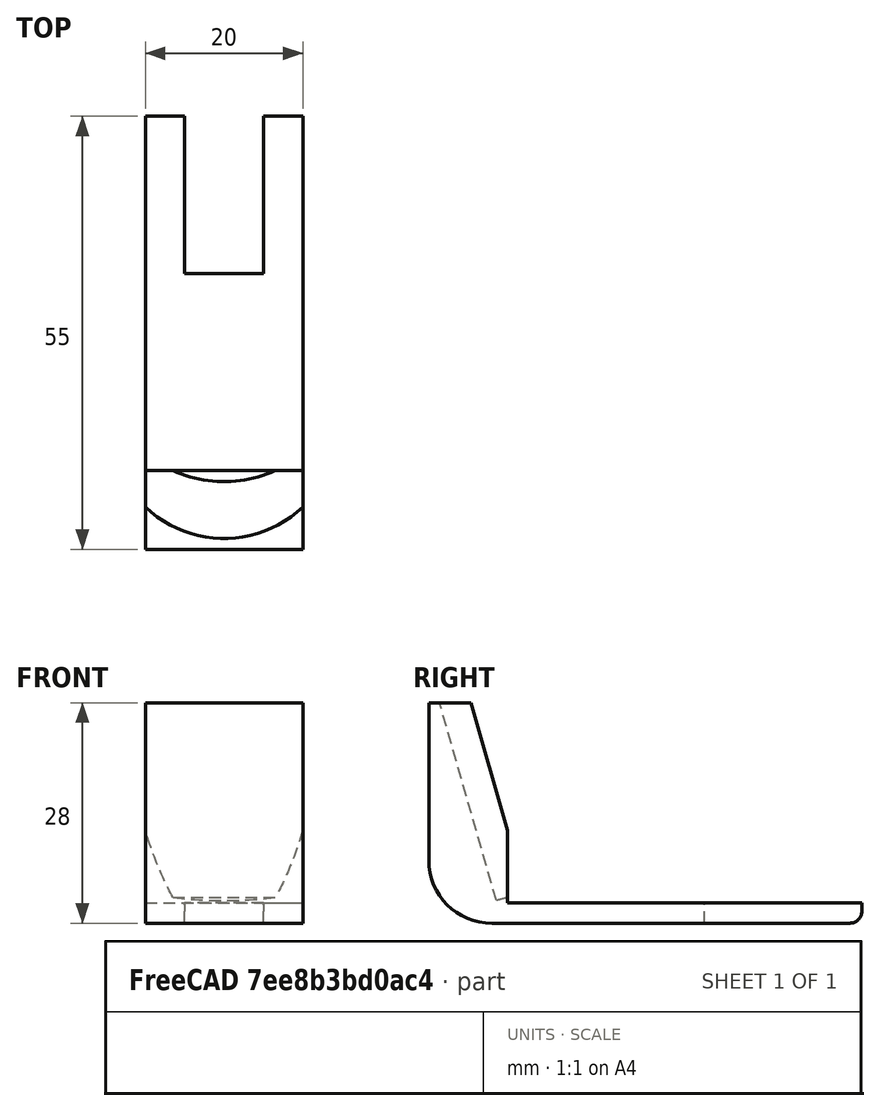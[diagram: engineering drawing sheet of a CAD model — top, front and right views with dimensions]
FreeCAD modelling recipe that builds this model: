
FCSTD DOCUMENT
Label: j-support_v1
objects: Part::Box×3, Part::Cut×2, Part::Fillet×2, Part::Cylinder×1, Part::Fuse×1
note: 9 computed .brp shape members not serialized (recipe doc carries the construction recipe); baked Part::Feature solids carry a one-line shape summary decoded from their .brp

FEATURE [Part::Box] Box  label="Box01"
  Height = 2.6
  Length = 20
  Width = 45
FEATURE [Part::Box] Box001  label="Box02"
  Height = 10
  Length = 10
  Placement = pos=(5,25,-3) rot=(0,0,1;0rad)
  Width = 25
FEATURE [Part::Cut] Cut  label="Patte"
  Base = -> Box
  Tool = -> Box001
FEATURE [Part::Box] Box002
  Height = 28
  Length = 20
  Placement = pos=(0,-10,0) rot=(0,0,1;0rad)
  Width = 10
FEATURE [Part::Fillet] Fillet
  Base = -> Box002
  Edges = 1 edges r=8: [Edge9]
FEATURE [Part::Cylinder] Cylinder
  Angle = 360
  Height = 27
  Placement = pos=(10,13,7) rot=(1,0,0;0.279252rad)
  Radius = 15
FEATURE [Part::Cut] Cut001
  Base = -> Fillet
  Tool = -> Cylinder
FEATURE [Part::Fuse] Fusion
  Base = -> Cut001
  Tool = -> Cut
FEATURE [Part::Fillet] Fillet001
  Base = -> Fusion
  Edges = 2 edges r=1.5: [Edge34,Edge35]
